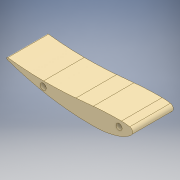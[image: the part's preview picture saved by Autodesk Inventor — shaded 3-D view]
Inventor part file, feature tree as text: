
AUTODESK INVENTOR PART (.ipt)
format: ipt  version: 2018.2 (Build 222227000, 227)  size: 125,440 bytes
history: native  units: mm
features: extrude x1, sketch x1, projected_geometry x1
ambient origin geometry x8: Origin, YZ Plane, XZ Plane, XY Plane, X Axis, Y Axis, Z Axis, Center Point
bodies: Body1 (feature_tree)
feature tree (3):
  extrude  "押し出し1"  Depth=40.2mm TaperAngle=0.0deg
  sketch  "スケッチ1"
  projected_geometry  "投影ループ1"
